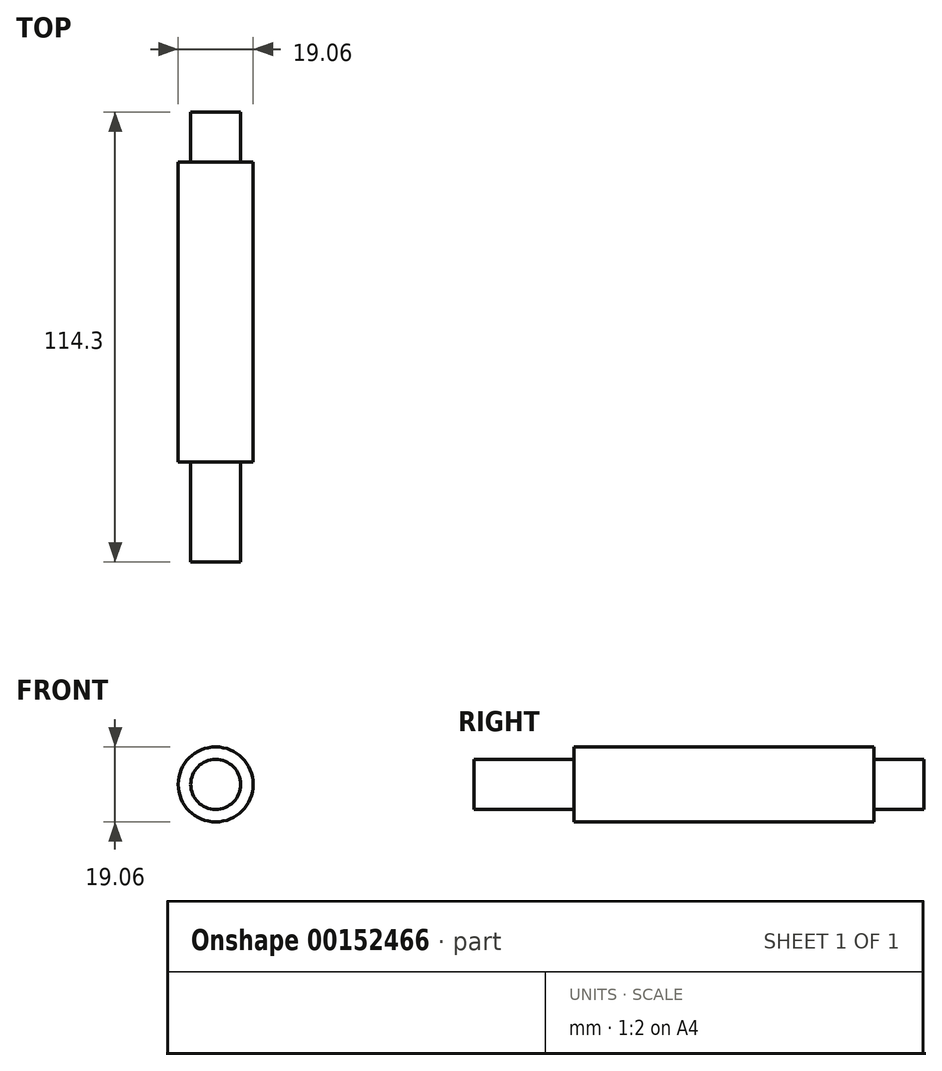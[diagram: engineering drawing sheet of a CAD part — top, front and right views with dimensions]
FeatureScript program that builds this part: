
annotation { "Feature Type Name" : "Feature", "Feature Type Description" : "" }
export const myFeature = defineFeature(function(context is Context, id is Id, definition is map)
    precondition{}
    {
        {
            var Q0;
            Q0=qCreatedBy(makeId("Front.planeOp"),FACE);
            var sketch = newSketch(context, id + "F0", { "sketchPlane" : qUnion([Q0])});
            skCircle(sketch, "E0", {"center": v(0, 0) * mm, "radius": 6.35 * mm});
            skSolve(sketch);
        }
        {
            var Q0;
            Q0=qSketchRegion(id+"F0",true);
            extrude(context, id + "F1", {"entities" : qUnion([Q0]), "depth" : 25.4 * mm});
        }
        {
            var Q0;
            Q0=qCreatedBy(makeId("Front.planeOp"),FACE);
            var sketch = newSketch(context, id + "F2", { "sketchPlane" : qUnion([Q0])});
            skCircle(sketch, "E1", {"center": v(0, 0) * mm, "radius": 9.53 * mm});
            skSolve(sketch);
        }
        {
            var Q0;
            Q0=qSketchRegion(id+"F2",true);
            extrude(context, id + "F3", {"entities" : qUnion([Q0]), "operationType" : NewBodyOperationType.ADD, "oppositeDirection" : true, "depth" : 76.2 * mm});
        }
        {
            var Q0;
            Q0=makeQuery(id+"F3.opExtrude","CAP_FACE",FACE,{"disambiguationData":[OSD([sQuery(id+"F2.wireOp",EDGE,"E1")])],"isStart":false});
            var sketch = newSketch(context, id + "F4", { "sketchPlane" : qUnion([Q0])});
            skCircle(sketch, "E2", {"center": v(0, 0) * mm, "radius": 6.35 * mm});
            skSolve(sketch);
        }
        {
            var Q0;
            Q0=qSketchRegion(id+"F4",true);
            extrude(context, id + "F5", {"entities" : qUnion([Q0]), "operationType" : NewBodyOperationType.ADD, "depth" : 12.7 * mm});
        }
    });
